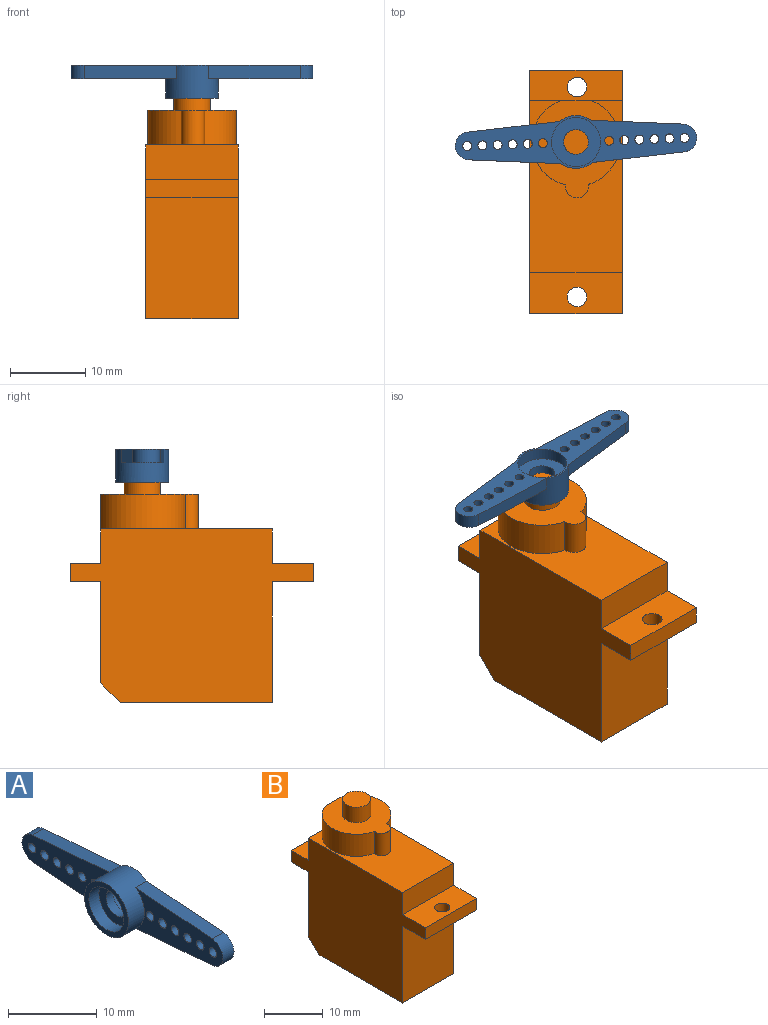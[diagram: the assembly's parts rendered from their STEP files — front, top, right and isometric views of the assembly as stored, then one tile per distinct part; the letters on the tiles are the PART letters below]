
ASSEMBLY  parts=2 mates=1
PART A: 28 faces, bbox 4.3x32x7 mm
  f0: cylinder r=1.65mm len=3.3mm, axis (1,0,0), area 11.8mm2, adj f24,f27
  f1: plane 13.89x5.59mm, normal (-1,0,0), area 49mm2, adj f3,f4,f5,f6,f17,f18,f19,f20
  f2: plane 13.89x5.59mm, normal (-1,0,0), area 49mm2, adj f6,f7,f8,f9,f11,f12,f13,f14
  f3: plane 12.19x1.78mm, normal (0,0.08,-1), area 21.7mm2, adj f1,f4,f6,f10
  f4: cylinder r=1.84mm len=3.67mm, axis (-1,0,0), area 9.8mm2, adj f1,f3,f5,f10
  f5: plane 12.19x1.78mm, normal (0,0.08,1), area 21.7mm2, adj f1,f4,f6,f10
  f6: cylinder r=3.5mm len=7mm, axis (-1,0,0), area 71.9mm2, adj f1,f2,f3,f5,f7,f9,f10,f23
  f7: plane 12.19x1.78mm, normal (0,-0.08,1), area 21.7mm2, adj f2,f6,f8,f10
  f8: cylinder r=1.84mm len=3.67mm, axis (-1,0,0), area 9.8mm2, adj f2,f7,f9,f10
  f9: plane 12.19x1.78mm, normal (0,-0.08,-1), area 21.7mm2, adj f2,f6,f8,f10
  f10: plane 32x7mm, normal (1,0,0), area 103.4mm2, adj f3,f4,f5,f6,f7,f8,f9,f11
  f11: cylinder r=0.6mm len=1.78mm, axis (1,0,0), area 6.7mm2, adj f2,f10
  f12: cylinder r=0.6mm len=1.78mm, axis (1,0,0), area 6.7mm2, adj f2,f10
  f13: cylinder r=0.6mm len=1.78mm, axis (1,0,0), area 6.7mm2, adj f2,f10
  f14: cylinder r=0.6mm len=1.78mm, axis (1,0,0), area 6.7mm2, adj f2,f10
  f15: cylinder r=0.6mm len=1.78mm, axis (1,0,0), area 6.7mm2, adj f2,f10
  f16: cylinder r=0.6mm len=1.78mm, axis (1,0,0), area 6.7mm2, adj f2,f10
  f17: cylinder r=0.6mm len=1.78mm, axis (1,0,0), area 6.7mm2, adj f1,f10
  f18: cylinder r=0.6mm len=1.78mm, axis (1,0,0), area 6.7mm2, adj f1,f10
  f19: cylinder r=0.6mm len=1.78mm, axis (1,0,0), area 6.7mm2, adj f1,f10
  f20: cylinder r=0.6mm len=1.78mm, axis (1,0,0), area 6.7mm2, adj f1,f10
  f21: cylinder r=0.6mm len=1.78mm, axis (1,0,0), area 6.7mm2, adj f1,f10
  f22: cylinder r=0.6mm len=1.78mm, axis (1,0,0), area 6.7mm2, adj f1,f10
  f23: plane 7x7mm, normal (-1,0,0), area 14mm2, adj f6,f26
  f24: plane 6.5x6.5mm, normal (1,0,0), area 24.6mm2, adj f0,f25
  f25: cylinder r=3.25mm len=6.5mm, axis (1,0,0), area 32.4mm2, adj f10,f24
  f26: cylinder r=2.79mm len=5.58mm, axis (-1,0,0), area 27.8mm2, adj f23,f27
  f27: plane 5.58x5.58mm, normal (-1,0,0), area 15.9mm2, adj f0,f26
PART B: 23 faces, bbox 12.3x32.3x30.8 mm
  f0: plane 12.3x9.2mm, normal (0,1,0), area 74.9mm2, adj f2,f4,f6,f11,f14,f16,f17
  f1: plane 16x12.3mm, normal (0,-1,0), area 196.8mm2, adj f2,f4,f7,f9
  f2: plane 32.3x23mm, normal (-1,0,0), area 542.8mm2, adj f0,f1,f3,f5,f6,f7,f8,f9
  f3: plane 12.3x4.6mm, normal (0,-1,0), area 56.6mm2, adj f2,f4,f6,f8
  f4: plane 32.3x23mm, normal (1,0,0), area 542.8mm2, adj f0,f1,f3,f5,f6,f7,f8,f9
  f5: plane 13.4x12.3mm, normal (0,1,0), area 164.8mm2, adj f2,f4,f12,f20
  f6: plane 22.75x12.3mm, normal (0,0,1), area 169.3mm2, adj f0,f2,f3,f4,f14,f15,f16
  f7: plane 20.15x12.3mm, normal (0,0,-1), area 247.8mm2, adj f1,f2,f4,f20
  f8: plane 12.3x5.5mm, normal (0,0,1), area 62.3mm2, adj f2,f3,f4,f10,f21
  f9: plane 12.3x5.5mm, normal (0,0,-1), area 62.3mm2, adj f1,f2,f4,f10,f21
  f10: plane 12.3x2.4mm, normal (0,-1,0), area 29.5mm2, adj f2,f4,f8,f9
  f11: plane 12.3x4.05mm, normal (0,0,1), area 44.5mm2, adj f0,f2,f4,f13,f22
  f12: plane 12.3x4.05mm, normal (0,0,-1), area 44.5mm2, adj f2,f4,f5,f13,f22
  f13: plane 12.3x2.4mm, normal (0,1,0), area 29.5mm2, adj f2,f4,f11,f12
  f14: cylinder r=5.85mm len=11.18mm, axis (0,0,-1), area 68.6mm2, adj f0,f6,f15,f17
  f15: cylinder r=1.55mm len=4.6mm, axis (0,0,-1), area 24.2mm2, adj f6,f14,f16,f17
  f16: cylinder r=5.85mm len=11.11mm, axis (0,0,-1), area 67.5mm2, adj f0,f6,f15,f17
  f17: plane 12.9x11.7mm, normal (0,0,1), area 92.4mm2, adj f0,f14,f15,f16,f18
  f18: cylinder r=2.4mm len=4.8mm, axis (0,0,-1), area 48.3mm2, adj f17,f19
  f19: plane 4.8x4.8mm, normal (0,0,1), area 18.1mm2, adj f18
  f20: plane 12.3x2.6mm, normal (0,0.71,-0.71), area 45.2mm2, adj f2,f4,f5,f7
  f21: cylinder r=1.3mm len=2.6mm, axis (0,0,1), area 19.6mm2, adj f8,f9
  f22: cylinder r=1.3mm len=2.6mm, axis (0,0,1), area 19.6mm2, adj f11,f12
PLACE A rot(axis=(-0.57,-0.59,-0.57),118.8deg) t=(-0.13,4.3,31.75)mm
PLACE B at identity fixed
MATE revolute A.f0 <-> B.f14  axis (0,0,-1) through (-0.13,4.3,30.8)mm
